# Revit family: Shower-Drain_Cover-KOHLER-Tile-In-K-80650_1
name_source: partatom
category: Specialty Equipment
revit_build: Autodesk Revit 2017 (Build: 20160225_1515(x64)
units: mm (PartAtom-declared; Revit-internal decimal feet)

## family parameters
Cut with Voids When Loaded = No
Host = Face
OmniClass Number = 23.31.25.00
Part Type = Normal
Room Calculation Point = No
Round Connector Dimension = Use Diameter
Shared = No

## types (4) — shared parameters
ADA Compliant = No
Assembly Code = C1030200
Date Modified = 04/15/2021
Default Elevation = 0"
Description = 36 INCH TILE-IN THIN LINEAR DRAIN GRID
Height = 1 1/8"
Length = 1 5/16"
Manufacturer = KOHLER Co.
Master Format 2014 = 10 28 00
Master Format 2014 Name = Toilet, Bath, and Laundry Accessories
Material = Aluminum
Product Documentation Link = https://www.us.kohler.com
Product Name = TILE-IN
Product Page URL = http://www.us.kohler.com
URL = https://www.us.kohler.com
WaterSense Certified = No
Width = 36"

## per-type parameters (varying)
| type | Finish | Model | Type |
| 2MB-Vibrant Brushed Moderne Brass | Kohler-Metal-2MB-Vibrant_Brushed_Moderne_Brass | K-80650-2MB | 1 |
| BL-Matte Black | Kohler-Metal-BL-Matte_Black | K-80650-BL | 2 |
| BNK-Anodized Brushed Nickel | Kohler-Metal-BNK-Anodized_Brushed_Nickel | K-80650-BNK | 3 |
| SH-Bright Silver | Kohler-Metal-SH-Bright_Silver | K-80650-SH | 4 |

## geometry (parser evidence)
native form markers: Sweep x6
no freeform markers — native parametric forms only
